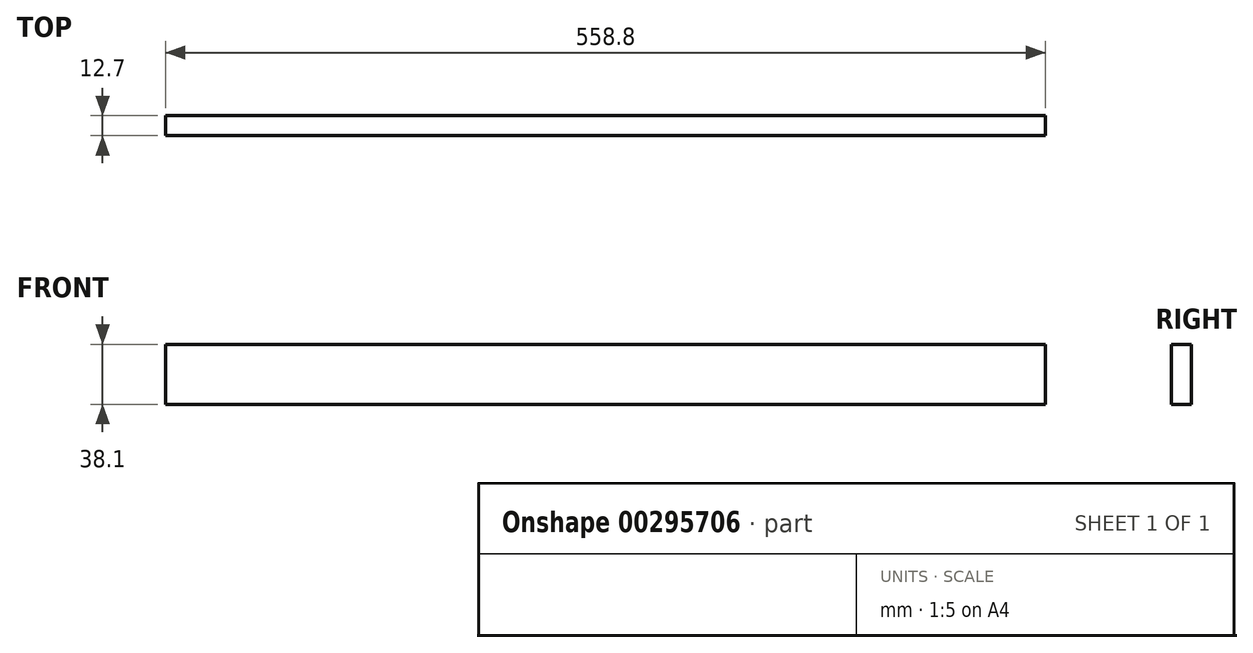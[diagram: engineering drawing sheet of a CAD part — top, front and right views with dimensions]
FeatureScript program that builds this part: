
annotation { "Feature Type Name" : "Feature", "Feature Type Description" : "" }
export const myFeature = defineFeature(function(context is Context, id is Id, definition is map)
    precondition{}
    {
        {
            var Q0;
            Q0=qCreatedBy(makeId("Front.planeOp"),FACE);
            var sketch = newSketch(context, id + "F0", { "sketchPlane" : qUnion([Q0])});
            skLineSegment(sketch, "E0.bottom", {"start": v(279.4, 19.05) * mm, "end": v(-279.4, 19.05) * mm});
            skLineSegment(sketch, "E0.top", {"start": v(279.4, -19.05) * mm, "end": v(-279.4, -19.05) * mm});
            skLineSegment(sketch, "E0.left", {"start": v(279.4, 19.05) * mm, "end": v(279.4, -19.05) * mm});
            skLineSegment(sketch, "E0.right", {"start": v(-279.4, 19.05) * mm, "end": v(-279.4, -19.05) * mm});
            skPoint(sketch, "E0.middle", {"position": v(0, 0) * mm});
            skSolve(sketch);
        }
        {
            var Q0;
            Q0 = qSketchRegion(id + "F0", true);
            extrude(context, id + "F1", {"entities" : qUnion([Q0]), "endBound" : BoundingType.SYMMETRIC, "depth" : 12.7 * mm});
        }
    });
